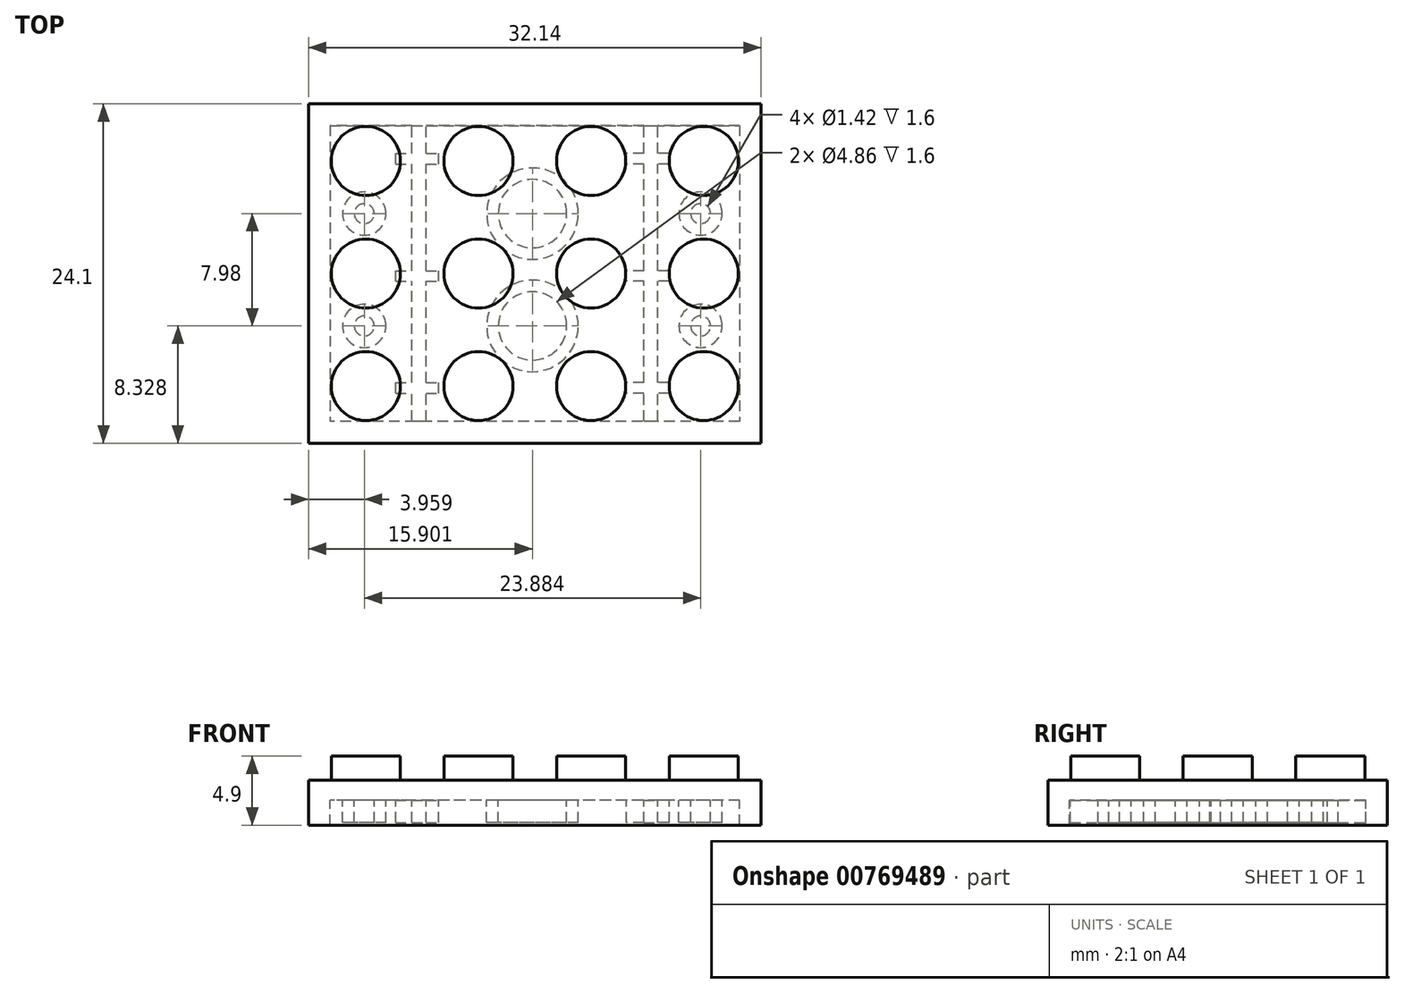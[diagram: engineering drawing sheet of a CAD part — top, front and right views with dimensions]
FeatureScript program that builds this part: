
annotation { "Feature Type Name" : "Feature", "Feature Type Description" : "" }
export const myFeature = defineFeature(function(context is Context, id is Id, definition is map)
    precondition{}
    {
        {
            var Q0;
            Q0=qCreatedBy(makeId("Front.planeOp"),FACE);
            var sketch = newSketch(context, id + "F0", { "sketchPlane" : qUnion([Q0])});
            skLineSegment(sketch, "E0.bottom", {"start": v(-2.07, 0) * mm, "end": v(30.07, 0) * mm});
            skLineSegment(sketch, "E0.top", {"start": v(-2.07, -3.18) * mm, "end": v(30.07, -3.18) * mm});
            skLineSegment(sketch, "E0.left", {"start": v(-2.07, 0) * mm, "end": v(-2.07, -3.18) * mm});
            skLineSegment(sketch, "E0.right", {"start": v(30.07, 0) * mm, "end": v(30.07, -3.18) * mm});
            skSolve(sketch);
        }
        {
            var Q0;
            Q0 = qSketchRegion(id + "F0", true);
            extrude(context, id + "F1", {"entities" : qUnion([Q0]), "depth" : 24.1 * mm, "offsetDistance" : 25 * mm});
        }
        {
            var Q0;
            Q0=qCreatedBy(makeId("Top.planeOp"),FACE);
            var sketch = newSketch(context, id + "F2", { "sketchPlane" : qUnion([Q0])});
            skCircle(sketch, "E1", {"center": v(2, -4.05) * mm, "radius": 2.45 * mm});
            skCircle(sketch, "E2", {"center": v(10, -4.05) * mm, "radius": 2.45 * mm});
            skCircle(sketch, "E3", {"center": v(18, -4.05) * mm, "radius": 2.45 * mm});
            skCircle(sketch, "E4", {"center": v(26, -4.05) * mm, "radius": 2.45 * mm});
            skCircle(sketch, "E5", {"center": v(26, -12.05) * mm, "radius": 2.45 * mm});
            skCircle(sketch, "E6", {"center": v(26, -20.05) * mm, "radius": 2.45 * mm});
            skCircle(sketch, "E7", {"center": v(18, -12.05) * mm, "radius": 2.45 * mm});
            skCircle(sketch, "E8", {"center": v(18, -20.05) * mm, "radius": 2.45 * mm});
            skCircle(sketch, "E9", {"center": v(10, -12.05) * mm, "radius": 2.45 * mm});
            skCircle(sketch, "E10", {"center": v(10, -20.05) * mm, "radius": 2.45 * mm});
            skCircle(sketch, "E11", {"center": v(2, -12.05) * mm, "radius": 2.45 * mm});
            skCircle(sketch, "E12", {"center": v(2, -20.05) * mm, "radius": 2.45 * mm});
            skSolve(sketch);
        }
        {
            var Q0;
            Q0 = qSketchRegion(id + "F2", true);
            extrude(context, id + "F3", {"entities" : qUnion([Q0]), "operationType" : NewBodyOperationType.ADD, "depth" : 1.72 * mm, "offsetDistance" : 25 * mm});
        }
        {
            var Q0;
            Q0=qCreatedBy(makeId("Top.planeOp"),FACE);
            var sketch = newSketch(context, id + "F4", { "sketchPlane" : qUnion([Q0])});
            skLineSegment(sketch, "E13.bottom", {"start": v(-0.54, -22.57) * mm, "end": v(28.54, -22.57) * mm});
            skLineSegment(sketch, "E13.top", {"start": v(-0.54, -1.53) * mm, "end": v(28.54, -1.53) * mm});
            skLineSegment(sketch, "E13.right", {"start": v(28.54, -22.57) * mm, "end": v(28.54, -1.53) * mm});
            skLineSegment(sketch, "E14", {"start": v(-0.54, -22.57) * mm, "end": v(-0.54, -1.53) * mm});
            skPoint(sketch, "E15.orphan", {"position": v(0, -22.57) * mm});
            skSolve(sketch);
        }
        {
            var Q0;
            Q0 = qSketchRegion(id + "F4", true);
            extrude(context, id + "F5", {"entities" : qUnion([Q0]), "operationType" : NewBodyOperationType.REMOVE, "oppositeDirection" : true, "depth" : 3.5 * mm, "offsetDistance" : 25 * mm});
        }
        {
            var Q0;
            Q0=qCreatedBy(makeId("Top.planeOp"),FACE);
            var sketch = newSketch(context, id + "F6", { "sketchPlane" : qUnion([Q0])});
            skLineSegment(sketch, "E16.bottom", {"start": v(-2.01, 0) * mm, "end": v(30.07, 0) * mm});
            skLineSegment(sketch, "E16.top", {"start": v(-2.01, -23.63) * mm, "end": v(30.07, -23.63) * mm});
            skLineSegment(sketch, "E16.left", {"start": v(-2.01, 0) * mm, "end": v(-2.01, -23.63) * mm});
            skLineSegment(sketch, "E16.right", {"start": v(30.07, 0) * mm, "end": v(30.07, -23.63) * mm});
            skSolve(sketch);
        }
        {
            var Q0;
            Q0 = qSketchRegion(id + "F6", true);
            extrude(context, id + "F7", {"entities" : qUnion([Q0]), "oppositeDirection" : true, "depth" : 1.4 * mm, "offsetDistance" : 25 * mm});
        }
        {
            var Q0;
            Q0=qCreatedBy(makeId("Top.planeOp"),FACE);
            var sketch = newSketch(context, id + "F8", { "sketchPlane" : qUnion([Q0])});
            skLineSegment(sketch, "E17.bottom", {"start": v(5.27, -22.53) * mm, "end": v(6.27, -22.53) * mm});
            skLineSegment(sketch, "E17.top", {"start": v(5.27, -1.53) * mm, "end": v(6.27, -1.53) * mm});
            skLineSegment(sketch, "E17.left", {"start": v(5.27, -22.53) * mm, "end": v(5.27, -1.53) * mm});
            skLineSegment(sketch, "E17.right", {"start": v(6.27, -22.53) * mm, "end": v(6.27, -1.53) * mm});
            skLineSegment(sketch, "E18.bottom", {"start": v(21.73, -22.53) * mm, "end": v(22.73, -22.53) * mm});
            skLineSegment(sketch, "E18.top", {"start": v(21.73, -1.53) * mm, "end": v(22.73, -1.53) * mm});
            skLineSegment(sketch, "E18.left", {"start": v(22.73, -22.53) * mm, "end": v(22.73, -1.53) * mm});
            skLineSegment(sketch, "E18.right", {"start": v(21.73, -22.53) * mm, "end": v(21.73, -1.53) * mm});
            skLineSegment(sketch, "E19.bottom", {"start": v(4.12, -20.55) * mm, "end": v(7.16, -20.55) * mm});
            skLineSegment(sketch, "E19.top", {"start": v(4.12, -19.8) * mm, "end": v(7.16, -19.8) * mm});
            skLineSegment(sketch, "E19.left", {"start": v(4.12, -20.55) * mm, "end": v(4.12, -19.8) * mm});
            skLineSegment(sketch, "E19.right", {"start": v(7.16, -20.55) * mm, "end": v(7.16, -19.8) * mm});
            skLineSegment(sketch, "E20.bottom", {"start": v(4.12, -12.6) * mm, "end": v(7.16, -12.6) * mm});
            skLineSegment(sketch, "E20.top", {"start": v(4.12, -11.85) * mm, "end": v(7.16, -11.85) * mm});
            skLineSegment(sketch, "E20.left", {"start": v(4.12, -12.6) * mm, "end": v(4.12, -11.85) * mm});
            skLineSegment(sketch, "E20.right", {"start": v(7.16, -12.6) * mm, "end": v(7.16, -11.85) * mm});
            skLineSegment(sketch, "E21.bottom", {"start": v(4.12, -4.26) * mm, "end": v(7.16, -4.26) * mm});
            skLineSegment(sketch, "E21.top", {"start": v(4.12, -3.51) * mm, "end": v(7.16, -3.51) * mm});
            skLineSegment(sketch, "E21.left", {"start": v(4.12, -4.26) * mm, "end": v(4.12, -3.51) * mm});
            skLineSegment(sketch, "E21.right", {"start": v(7.16, -4.26) * mm, "end": v(7.16, -3.51) * mm});
            skLineSegment(sketch, "E22.MirrorCS", {"start": v(23.55, -20.55) * mm, "end": v(20.5, -20.55) * mm});
            skLineSegment(sketch, "E23.MirrorCS", {"start": v(23.55, -19.8) * mm, "end": v(20.5, -19.8) * mm});
            skLineSegment(sketch, "E24.MirrorCS", {"start": v(23.55, -20.55) * mm, "end": v(23.55, -19.8) * mm});
            skLineSegment(sketch, "E25.MirrorCS", {"start": v(23.55, -12.6) * mm, "end": v(20.5, -12.6) * mm});
            skLineSegment(sketch, "E26.MirrorCS", {"start": v(23.55, -12.6) * mm, "end": v(23.55, -11.85) * mm});
            skLineSegment(sketch, "E27.MirrorCS", {"start": v(20.5, -12.6) * mm, "end": v(20.5, -11.85) * mm});
            skLineSegment(sketch, "E28.MirrorCS", {"start": v(23.55, -11.85) * mm, "end": v(20.5, -11.85) * mm});
            skLineSegment(sketch, "E29.MirrorCS", {"start": v(23.55, -4.26) * mm, "end": v(20.5, -4.26) * mm});
            skLineSegment(sketch, "E30.MirrorCS", {"start": v(23.55, -3.51) * mm, "end": v(20.5, -3.51) * mm});
            skLineSegment(sketch, "E31.MirrorCS", {"start": v(23.55, -4.26) * mm, "end": v(23.55, -3.51) * mm});
            skCircle(sketch, "E32", {"center": v(1.89, -7.8) * mm, "radius": 1.54 * mm});
            skCircle(sketch, "E33", {"center": v(1.89, -7.8) * mm, "radius": 0.71 * mm});
            skCircle(sketch, "E34", {"center": v(1.89, -15.77) * mm, "radius": 1.54 * mm});
            skCircle(sketch, "E35", {"center": v(1.89, -15.77) * mm, "radius": 0.71 * mm});
            skCircle(sketch, "E36.MirrorC", {"center": v(25.77, -15.77) * mm, "radius": 1.54 * mm});
            skCircle(sketch, "E37.MirrorC", {"center": v(25.77, -15.77) * mm, "radius": 0.71 * mm});
            skCircle(sketch, "E38.MirrorC", {"center": v(25.77, -7.8) * mm, "radius": 1.54 * mm});
            skCircle(sketch, "E39.MirrorC", {"center": v(25.77, -7.8) * mm, "radius": 0.71 * mm});
            skLineSegment(sketch, "E40", {"start": v(20.5, -4.26) * mm, "end": v(20.5, -3.51) * mm});
            skLineSegment(sketch, "E41", {"start": v(20.5, -20.55) * mm, "end": v(20.5, -19.8) * mm});
            skCircle(sketch, "E42", {"center": v(13.83, -15.77) * mm, "radius": 3.25 * mm});
            skCircle(sketch, "E43", {"center": v(13.83, -7.8) * mm, "radius": 3.25 * mm});
            skCircle(sketch, "E44", {"center": v(13.83, -15.77) * mm, "radius": 2.43 * mm});
            skCircle(sketch, "E45", {"center": v(13.83, -7.8) * mm, "radius": 2.43 * mm});
            skSolve(sketch);
        }
        {
            var Q0;
            Q0 = qSketchRegion(id + "F8", true);
            extrude(context, id + "F9", {"entities" : qUnion([Q0]), "operationType" : NewBodyOperationType.ADD, "oppositeDirection" : true, "depth" : 3 * mm, "offsetDistance" : 25 * mm});
        }
    });
